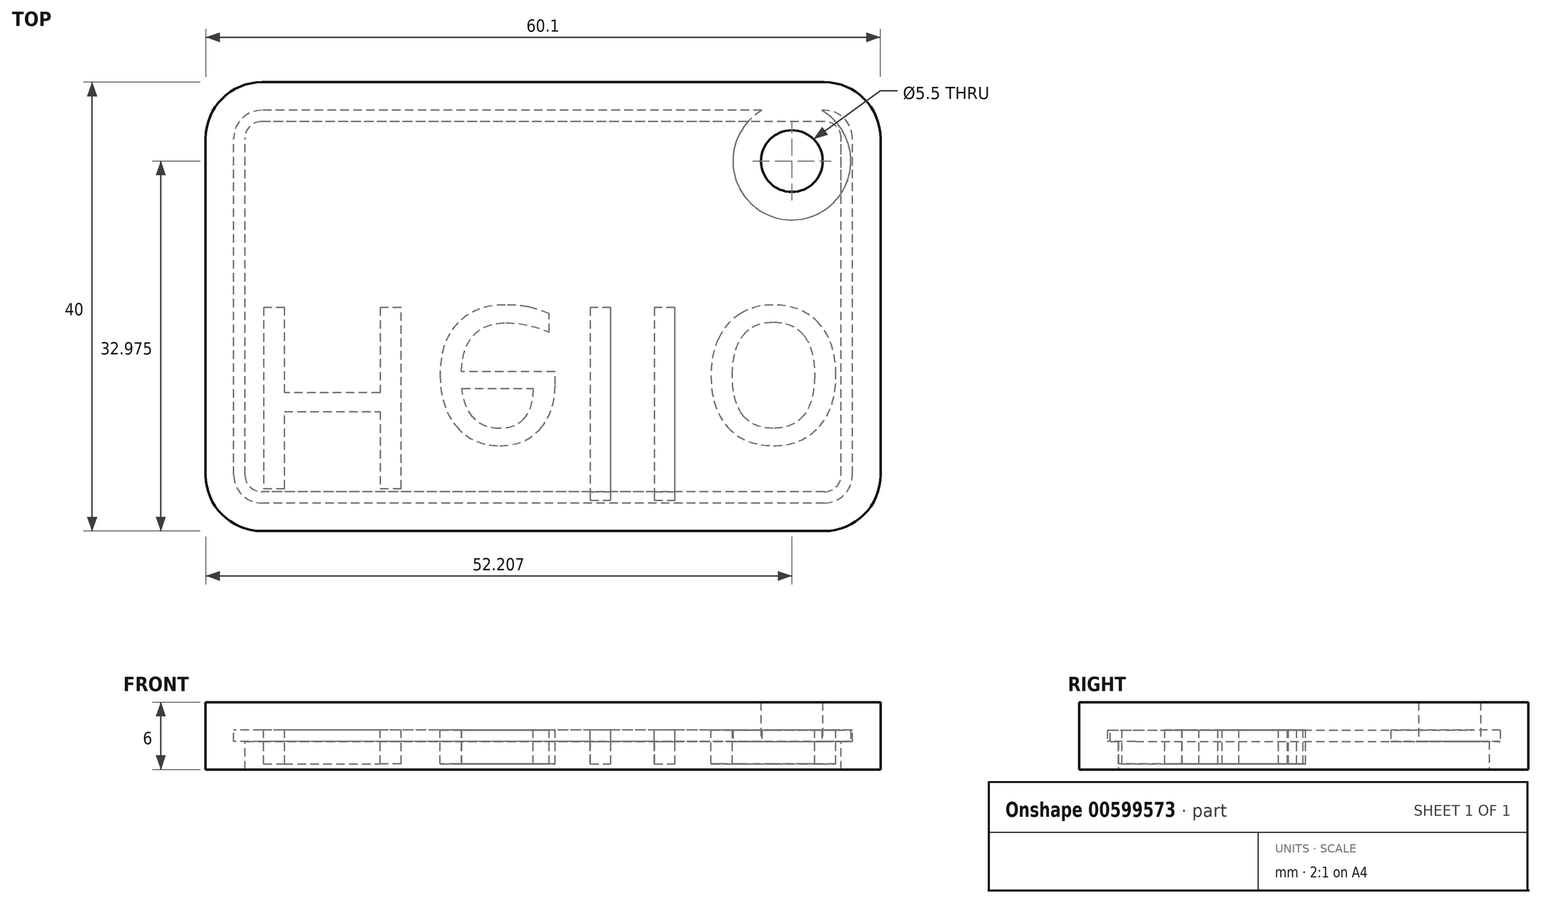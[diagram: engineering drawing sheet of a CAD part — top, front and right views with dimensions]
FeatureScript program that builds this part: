
annotation { "Feature Type Name" : "Feature", "Feature Type Description" : "" }
export const myFeature = defineFeature(function(context is Context, id is Id, definition is map)
    precondition{}
    {
        {
            var Q0;
            Q0=qCreatedBy(makeId("Top.planeOp"),FACE);
            var sketch = newSketch(context, id + "F0", { "sketchPlane" : qUnion([Q0])});
            skLineSegment(sketch, "E0.bottom", {"start": v(30.05, -20) * mm, "end": v(-30.05, -20) * mm});
            skLineSegment(sketch, "E0.top", {"start": v(30.05, 20) * mm, "end": v(-30.05, 20) * mm});
            skLineSegment(sketch, "E0.left", {"start": v(30.05, -20) * mm, "end": v(30.05, 20) * mm});
            skLineSegment(sketch, "E0.right", {"start": v(-30.05, -20) * mm, "end": v(-30.05, 20) * mm});
            skPoint(sketch, "E0.middle", {"position": v(0, 0) * mm});
            skSolve(sketch);
        }
        {
            var Q0;
            Q0=makeQuery(id+"F0.imprint","IMPRINT",FACE,{"disambiguationData":[TD([[makeQuery(id+"F0.imprint","IMPRINT",EDGE,{"derivedFrom":sQuery(id+"F0.wireOp",EDGE,"E0.bottom")}),-1.0]])]});
            extrude(context, id + "F1", {"entities" : qUnion([Q0]), "depth" : 6 * mm, "offsetDistance" : 25 * mm});
        }
        {
            var Q0;
            Q0=makeQuery(id+"F1.opExtrude","SWEPT_EDGE",EDGE,{"disambiguationData":[OSD([sQuery(id+"F0.wireOp",EDGE,"E0.top"),sQuery(id+"F0.wireOp",EDGE,"E0.right")])]});
            var Q1;
            Q1=makeQuery(id+"F1.opExtrude","SWEPT_EDGE",EDGE,{"disambiguationData":[OSD([sQuery(id+"F0.wireOp",EDGE,"E0.top"),sQuery(id+"F0.wireOp",EDGE,"E0.left")])]});
            var Q2;
            Q2=makeQuery(id+"F1.opExtrude","SWEPT_EDGE",EDGE,{"disambiguationData":[OSD([sQuery(id+"F0.wireOp",EDGE,"E0.bottom"),sQuery(id+"F0.wireOp",EDGE,"E0.left")])]});
            var Q3;
            Q3=makeQuery(id+"F1.opExtrude","SWEPT_EDGE",EDGE,{"disambiguationData":[OSD([sQuery(id+"F0.wireOp",EDGE,"E0.bottom"),sQuery(id+"F0.wireOp",EDGE,"E0.right")])]});
            fillet(context, id + "F2", {"entities" : qUnion([Q0, Q1, Q2, Q3]), "radius" : 5 * mm, "tangentPropagation" : true, "allowEdgeOverflow" : false});
        }
        {
            var Q0;
            Q0=makeQuery(id+"F1.opExtrude","CAP_FACE",FACE,{"disambiguationData":[OSD([sQuery(id+"F0.wireOp",EDGE,"E0.bottom"),sQuery(id+"F0.wireOp",EDGE,"E0.top"),sQuery(id+"F0.wireOp",EDGE,"E0.left"),sQuery(id+"F0.wireOp",EDGE,"E0.right")])],"isStart":true});
            shell(context, id + "F3", {"entities" : qUnion([Q0]), "thickness" : 3.5 * mm});
        }
        {
            var Q0;
            Q0=makeQuery(id+"F3.opShell","OFFSET_FACE",FACE,{"disambiguationData":[OSD([sQuery(id+"F0.wireOp",EDGE,"E0.bottom"),sQuery(id+"F0.wireOp",EDGE,"E0.top"),sQuery(id+"F0.wireOp",EDGE,"E0.left"),sQuery(id+"F0.wireOp",EDGE,"E0.right")])]});
            extrude(context, id + "F4", {"entities" : qUnion([Q0]), "operationType" : NewBodyOperationType.ADD, "depth" : -3 * mm, "offsetDistance" : 25 * mm});
        }
        {
            var Q0;
            Q0=makeQuery(id+"F3.opShell","OFFSET_FACE",FACE,{"disambiguationData":[OSD([sQuery(id+"F0.wireOp",EDGE,"E0.bottom"),sQuery(id+"F0.wireOp",EDGE,"E0.top"),sQuery(id+"F0.wireOp",EDGE,"E0.left"),sQuery(id+"F0.wireOp",EDGE,"E0.right")])]});
            var sketch = newSketch(context, id + "F5", { "sketchPlane" : qUnion([Q0])});
            skCircle(sketch, "E1", {"center": v(22.16, -12.98) * mm, "radius": 3.84 * mm});
            skSolve(sketch);
        }
        {
            var Q0;
            Q0=sQuery(id+"F5.wireOp",VERTEX,"E1.center");
            var Q1;
            Q1=makeQuery(id+"F1.opExtrude","SWEPT_BODY",BODY,{"disambiguationData":[OSD([sQuery(id+"F0.wireOp",EDGE,"E0.bottom"),sQuery(id+"F0.wireOp",EDGE,"E0.top"),sQuery(id+"F0.wireOp",EDGE,"E0.left"),sQuery(id+"F0.wireOp",EDGE,"E0.right")])]});
            hole(context, id + "F6", {"style" : HoleStyle.SIMPLE, "endStyle" : HoleEndStyle.BLIND, "holeDiameter" : 5.5 * mm, "majorDiameter" : 5 * mm, "holeDepth" : 12 * mm, "isTappedThrough" : true, "tappedDepth" : 12 * mm, "tapClearance" : 3, "locations" : qUnion([Q0]), "scope" : qUnion([Q1])});
        }
        {
            var Q0;
            Q0=makeQuery(id+"F3.opShell","OFFSET_FACE",FACE,{"disambiguationData":[OSD([sQuery(id+"F0.wireOp",EDGE,"E0.bottom"),sQuery(id+"F0.wireOp",EDGE,"E0.top"),sQuery(id+"F0.wireOp",EDGE,"E0.left"),sQuery(id+"F0.wireOp",EDGE,"E0.right")])]});
            shell(context, id + "F7", {"entities" : qUnion([Q0]), "thickness" : 2.5 * mm});
        }
        {
            var Q0;
            {var subQ0=sQuery(id+"F0.wireOp",EDGE,"E0.right");var subQ1=sQuery(id+"F0.wireOp",EDGE,"E0.left");var subQ2=sQuery(id+"F0.wireOp",EDGE,"E0.top");var subQ3=sQuery(id+"F0.wireOp",EDGE,"E0.bottom");Q0=makeQuery(id+"F7.opShell","OFFSET_FACE",FACE,{"disambiguationData":[OSD([subQ3,subQ2,subQ1,subQ0]),TDD([makeQuery(id+"F1.opExtrude","CAP_FACE",FACE,{"disambiguationData":[OSD([subQ3,subQ2,subQ1,subQ0])],"isStart":false})])]});}
            var sketch = newSketch(context, id + "F8", { "sketchPlane" : qUnion([Q0])});
            skText(sketch, "E2", { "text": "Hello\n", "fontName": "OpenSans-Regular.ttf"});
            const initialGuessF8  = {"E2": [-0.02712, 7e-05, 1, 0, 0.01628]};
            skSetInitialGuess(sketch, initialGuessF8);
            skSolve(sketch);
        }
        {
            var Q0;
            Q0 = qSketchRegion(id + "F8", true);
            extrude(context, id + "F9", {"entities" : qUnion([Q0]), "operationType" : NewBodyOperationType.ADD, "depth" : 3 * mm, "offsetDistance" : 25 * mm});
        }
    });
